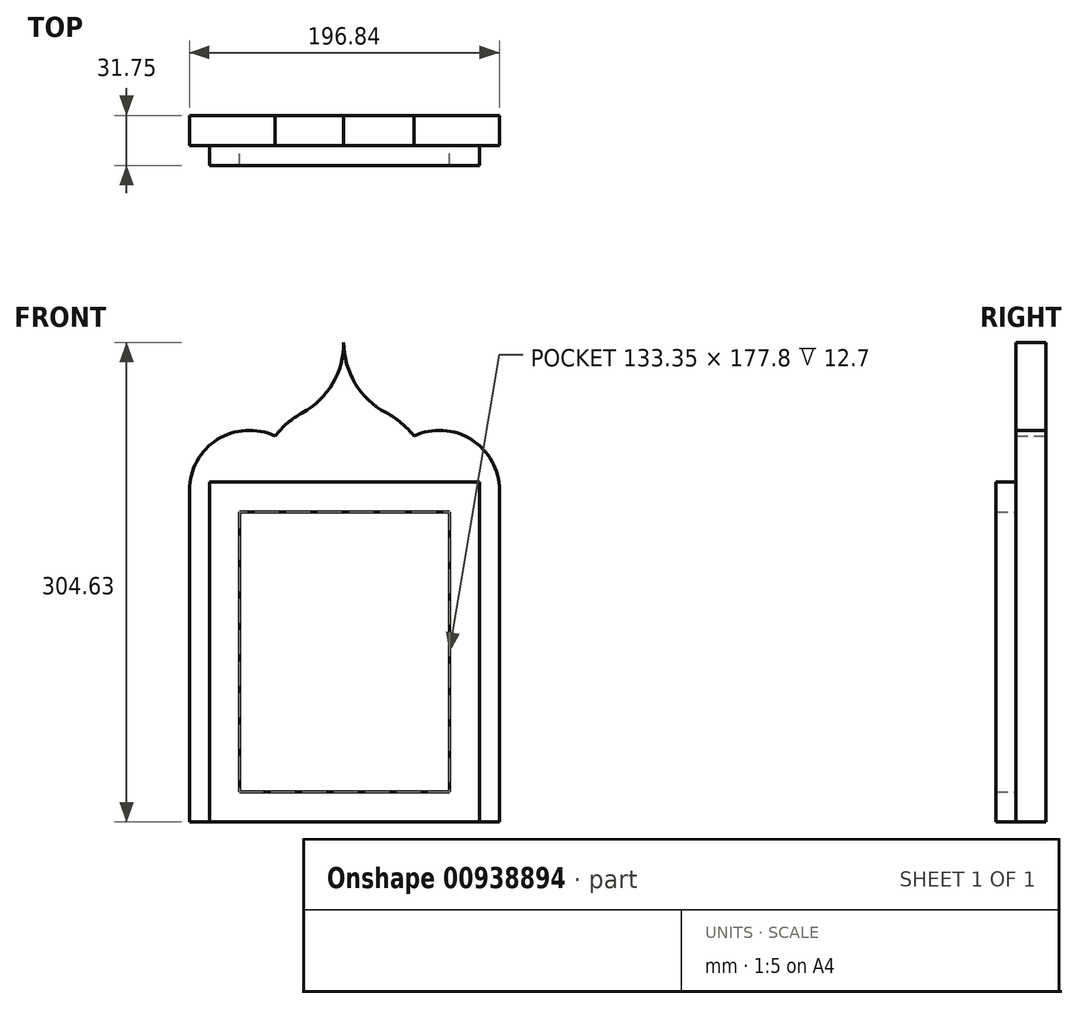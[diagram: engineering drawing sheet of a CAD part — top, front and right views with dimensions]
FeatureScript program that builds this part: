
annotation { "Feature Type Name" : "Feature", "Feature Type Description" : "" }
export const myFeature = defineFeature(function(context is Context, id is Id, definition is map)
    precondition{}
    {
        {
            var Q0;
            Q0=qCreatedBy(makeId("Front.planeOp"),FACE);
            var sketch = newSketch(context, id + "F0", { "sketchPlane" : qUnion([Q0])});
            skLineSegment(sketch, "E0.bottom", {"start": v(98.43, -133.35) * mm, "end": v(-98.42, -133.35) * mm});
            skLineSegment(sketch, "E0.left", {"start": v(98.43, -133.35) * mm, "end": v(98.43, 92.08) * mm});
            skLineSegment(sketch, "E0.right", {"start": v(-98.42, -133.35) * mm, "end": v(-98.43, 92.08) * mm});
            skPoint(sketch, "E0.middle", {"position": v(0, 0) * mm});
            skPoint(sketch, "E1", {"position": v(-98.43, 92.08) * mm});
            skPoint(sketch, "E2", {"position": v(-41.28, 92.08) * mm});
            skPoint(sketch, "E3", {"position": v(41.28, 92.08) * mm});
            skPoint(sketch, "E4", {"position": v(98.43, 92.08) * mm});
            skPoint(sketch, "E5.orphan", {"position": v(98.42, 133.35) * mm});
            skPoint(sketch, "E6.orphan", {"position": v(-98.43, 133.35) * mm});
            skPoint(sketch, "E7.center.orphan", {"position": v(-69.85, 92.08) * mm});
            skPoint(sketch, "E8.center.orphan", {"position": v(0, 92.08) * mm});
            skPoint(sketch, "E9.center.orphan", {"position": v(69.85, 92.08) * mm});
            skArc(sketch, "E10", {"start": v(44.06, 111.87) * mm, "mid": v(36, 120.22) * mm, "end": v(26.4, 126.73) * mm});
            skPoint(sketch, "E10.centerSnap0", {"position": v(0, 133.35) * mm});
            skArc(sketch, "E11", {"start": v(-44.06, 111.87) * mm, "mid": v(-80.72, 109.6) * mm, "end": v(-98.43, 77.42) * mm});
            skArc(sketch, "E12", {"start": v(98.43, 77.42) * mm, "mid": v(80.72, 109.6) * mm, "end": v(44.06, 111.87) * mm});
            skPoint(sketch, "E13", {"position": v(-98.43, 77.42) * mm});
            skPoint(sketch, "E14", {"position": v(-44.06, 111.87) * mm});
            skPoint(sketch, "E15", {"position": v(44.06, 111.87) * mm});
            skPoint(sketch, "E16", {"position": v(98.43, 77.42) * mm});
            skArc(sketch, "E17", {"start": v(-0.43, 171.28) * mm, "mid": v(6.85, 145.31) * mm, "end": v(26.4, 126.73) * mm});
            skArc(sketch, "E18", {"start": v(-26.85, 126.49) * mm, "mid": v(-7.47, 145.25) * mm, "end": v(-0.43, 171.28) * mm});
            skPoint(sketch, "E19", {"position": v(-0.43, 171.28) * mm});
            skPoint(sketch, "E20", {"position": v(-26.85, 126.49) * mm});
            skPoint(sketch, "E21", {"position": v(26.4, 126.73) * mm});
            skArc(sketch, "E22.trimOffspring", {"start": v(-26.85, 126.49) * mm, "mid": v(-36.2, 120.06) * mm, "end": v(-44.06, 111.87) * mm});
            skSolve(sketch);
        }
        {
            var Q0;
            Q0 = qSketchRegion(id + "F0", true);
            extrude(context, id + "F1", {"entities" : qUnion([Q0]), "depth" : 19.05 * mm, "offsetDistance" : 25.4 * mm});
        }
        {
            var Q0;
            Q0=makeQuery(id+"F1.opExtrude","CAP_FACE",FACE,{"disambiguationData":[OSD([sQuery(id+"F0.wireOp",EDGE,"E0.bottom"),sQuery(id+"F0.wireOp",EDGE,"E0.left"),sQuery(id+"F0.wireOp",EDGE,"E0.right"),sQuery(id+"F0.wireOp",EDGE,"0SvJAVyy-UBuE-smbQ-L2yJ-5kaccnmKHyLX"),sQuery(id+"F0.wireOp",EDGE,"kSu48o60-3X1s-JAuV-3dwp-a7h1acsQaTDZ"),sQuery(id+"F0.wireOp",EDGE,"urfQ2LqI-bHUF-Dr9B-PCSo-ZHHZ8GKUOPEq"),sQuery(id+"F0.wireOp",EDGE,"7e23a14f-d31e-43d3-ab45-3d8b74d9af6c.filletArc"),sQuery(id+"F0.wireOp",EDGE,"bec49634-9b3d-44c2-b041-284ac3cb24c7.filletArc")])],"isStart":false});
            var sketch = newSketch(context, id + "F2", { "sketchPlane" : qUnion([Q0])});
            skPoint(sketch, "E23", {"position": v(0, 0) * mm});
            skPoint(sketch, "E24.orphan", {"position": v(0, 133.35) * mm});
            skPoint(sketch, "E25.end.orphan", {"position": v(0, -133.35) * mm});
            skLineSegment(sketch, "E26", {"start": v(98.43, -133.35) * mm, "end": v(-98.42, -133.35) * mm});
            skPoint(sketch, "E27.middle", {"position": v(0, -13.67) * mm});
            skPoint(sketch, "E28", {"position": v(-85.73, -133.35) * mm});
            skPoint(sketch, "E29", {"position": v(69.85, 92.08) * mm});
            skPoint(sketch, "E30", {"position": v(-85.73, 92.08) * mm});
            skPoint(sketch, "E31", {"position": v(69.85, -133.35) * mm});
            skPoint(sketch, "E32", {"position": v(0, -25.4) * mm});
            skPoint(sketch, "E33", {"position": v(0, 82.55) * mm});
            skPoint(sketch, "E34", {"position": v(85.73, 82.55) * mm});
            skLineSegment(sketch, "E35.bottom", {"start": v(-85.73, -133.35) * mm, "end": v(85.73, -133.35) * mm});
            skLineSegment(sketch, "E35.top", {"start": v(-85.73, 82.55) * mm, "end": v(85.73, 82.55) * mm});
            skLineSegment(sketch, "E35.left", {"start": v(-85.73, -133.35) * mm, "end": v(-85.73, 82.55) * mm});
            skLineSegment(sketch, "E35.right", {"start": v(85.73, -133.35) * mm, "end": v(85.73, 82.55) * mm});
            skPoint(sketch, "E36", {"position": v(-66.68, -114.3) * mm});
            skPoint(sketch, "E37", {"position": v(66.68, 63.5) * mm});
            skLineSegment(sketch, "E38.bottom", {"start": v(-66.68, -114.3) * mm, "end": v(66.68, -114.3) * mm});
            skLineSegment(sketch, "E38.top", {"start": v(-66.68, 63.5) * mm, "end": v(66.68, 63.5) * mm});
            skLineSegment(sketch, "E38.left", {"start": v(-66.68, -114.3) * mm, "end": v(-66.68, 63.5) * mm});
            skLineSegment(sketch, "E38.right", {"start": v(66.68, -114.3) * mm, "end": v(66.68, 63.5) * mm});
            skSolve(sketch);
        }
        {
            var Q0;
            Q0 = qSketchRegion(id + "F2", true);
            extrude(context, id + "F3", {"entities" : qUnion([Q0]), "operationType" : NewBodyOperationType.ADD, "depth" : 12.7 * mm, "offsetDistance" : 25.4 * mm});
        }
    });
